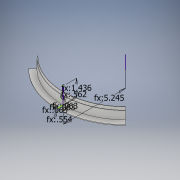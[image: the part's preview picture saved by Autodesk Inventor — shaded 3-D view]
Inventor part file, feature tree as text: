
AUTODESK INVENTOR PART (.ipt)
format: ipt  version: 2017 (Build 210142000, 142)  size: 183,296 bytes
history: native  units: in
note: dims shown in document units (in); Inventor stores cm internally (conversion verified against a paired STEP export)
features: sketch x5, extrude x4, revolve x2, plane x1
ambient origin geometry x8: Origin, YZ Plane, XZ Plane, XY Plane, X Axis, Y Axis, Z Axis, Center Point
bodies: Solid1 (feature_tree)
feature tree (12):
  revolve  "Revolution1"  [1 undecoded]
  plane  "Work Plane1"
  sketch  "Sketch2"  dims[d3=1.4364in d4=0.0625in]
  extrude  "Extrusion2"  Depth=0.0625in
  extrude  "Extrusion3"  TaperAngle=90.0deg  [1 undecoded]
  extrude  "Extrusion4"  Depth=0.375in
  extrude  "Extrusion5"  Depth=1.0in TaperAngle=0.0deg
  revolve  "Revolution2"  [1 undecoded]
  sketch  "Sketch1"  dims[d1=0.5536in d2=0.0625in]
  sketch  "Sketch3"  dims[d5=0.0625in d6=90.0deg]
  sketch  "Sketch4"  dims[d7=0.562in d8=0.375in]
  sketch  "Sketch5"  dims[d11=0.3125in d12=1.0in d13=0.0in d14=0.0156in d15=0.0in d16=0.25in d17=0.0625in d18=0.0in d19=135.0deg d20=0.0in d21=0.0in d22=0.75in d23=0.0312in d24=0.25in d25=0.25in d26=90.0deg]
note: 3 required parameter values undecoded (feature->parameter linkage not recoverable at this tier; creation-order binding heuristic only, values carry confidence <= 0.55)